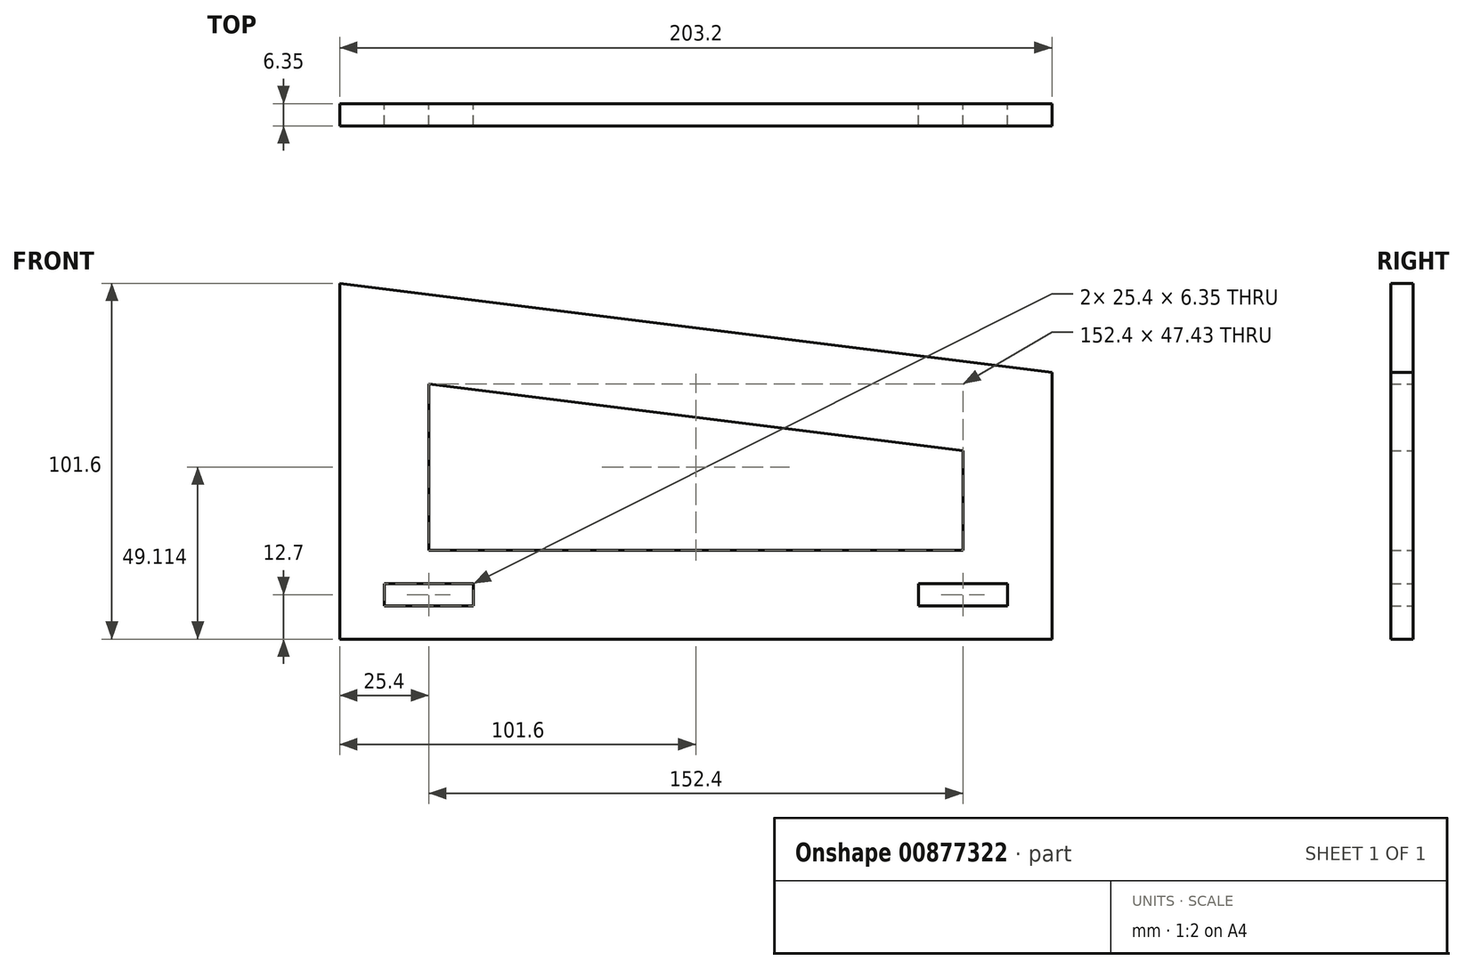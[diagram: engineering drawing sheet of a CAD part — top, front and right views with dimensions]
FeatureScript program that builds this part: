
annotation { "Feature Type Name" : "Feature", "Feature Type Description" : "" }
export const myFeature = defineFeature(function(context is Context, id is Id, definition is map)
    precondition{}
    {
        {
            var Q0;
            Q0=qCreatedBy(makeId("Front.planeOp"),FACE);
            var sketch = newSketch(context, id + "F0", { "sketchPlane" : qUnion([Q0])});
            skLineSegment(sketch, "E0", {"start": v(0, 0) * mm, "end": v(0, 101.6) * mm});
            skLineSegment(sketch, "E1", {"start": v(0, 101.6) * mm, "end": v(203.2, 76.2) * mm});
            skLineSegment(sketch, "E2", {"start": v(203.2, 76.2) * mm, "end": v(203.2, 0) * mm});
            skLineSegment(sketch, "E3", {"start": v(203.2, 0) * mm, "end": v(0, 0) * mm});
            skLineSegment(sketch, "E4.0", {"start": v(25.4, 72.83) * mm, "end": v(177.8, 53.78) * mm});
            skLineSegment(sketch, "E4.1", {"start": v(25.4, 25.4) * mm, "end": v(25.4, 72.83) * mm});
            skLineSegment(sketch, "E4.2", {"start": v(177.8, 25.4) * mm, "end": v(25.4, 25.4) * mm});
            skLineSegment(sketch, "E4.3", {"start": v(177.8, 53.78) * mm, "end": v(177.8, 25.4) * mm});
            skLineSegment(sketch, "E5.bottom", {"start": v(12.7, 15.88) * mm, "end": v(38.1, 15.87) * mm});
            skLineSegment(sketch, "E5.top", {"start": v(12.7, 9.52) * mm, "end": v(38.1, 9.52) * mm});
            skLineSegment(sketch, "E5.left", {"start": v(12.7, 15.88) * mm, "end": v(12.7, 9.52) * mm});
            skLineSegment(sketch, "E5.right", {"start": v(38.1, 15.88) * mm, "end": v(38.1, 9.52) * mm});
            skLineSegment(sketch, "E6", {"start": v(12.7, 15.88) * mm, "end": v(38.1, 9.52) * mm, "construction": true});
            skLineSegment(sketch, "E7", {"start": v(25.4, 12.7) * mm, "end": v(25.4, 0) * mm, "construction": true});
            skPoint(sketch, "E7.endSnap0", {"position": v(25.4, 9.52) * mm});
            skLineSegment(sketch, "E8", {"start": v(0, 12.7) * mm, "end": v(25.4, 12.7) * mm, "construction": true});
            skPoint(sketch, "E8.startSnap0", {"position": v(12.7, 12.7) * mm});
            skLineSegment(sketch, "E9.bottom", {"start": v(165.1, 15.87) * mm, "end": v(190.5, 15.87) * mm});
            skLineSegment(sketch, "E9.top", {"start": v(165.1, 9.52) * mm, "end": v(190.5, 9.52) * mm});
            skLineSegment(sketch, "E9.left", {"start": v(165.1, 15.87) * mm, "end": v(165.1, 9.52) * mm});
            skLineSegment(sketch, "E9.right", {"start": v(190.5, 15.87) * mm, "end": v(190.5, 9.52) * mm});
            skLineSegment(sketch, "E10", {"start": v(165.1, 15.88) * mm, "end": v(190.5, 9.52) * mm, "construction": true});
            skLineSegment(sketch, "E11", {"start": v(177.8, 12.7) * mm, "end": v(177.8, 0) * mm, "construction": true});
            skLineSegment(sketch, "E12", {"start": v(177.8, 12.7) * mm, "end": v(203.2, 12.7) * mm, "construction": true});
            skPoint(sketch, "E12.endSnap0", {"position": v(190.5, 12.7) * mm});
            skSolve(sketch);
        }
        {
            var Q0;
            Q0 = qSketchRegion(id + "F0", true);
            extrude(context, id + "F1", {"entities" : qUnion([Q0]), "depth" : 6.35 * mm, "offsetDistance" : 25.4 * mm});
        }
    });
